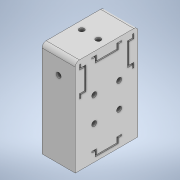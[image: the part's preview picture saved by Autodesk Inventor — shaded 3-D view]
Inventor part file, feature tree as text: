
AUTODESK INVENTOR PART (.ipt)
format: ipt  version: 2021 (Build 250183000, 183)  size: 275,968 bytes
history: native  units: mm
features: extrude x4, sketch x4, other x3
ambient origin geometry x8: Origin, YZ Plane, XZ Plane, XY Plane, X Axis, Y Axis, Z Axis, Center Point
bodies: Solid1 (feature_tree)
feature tree (11):
  other  "din_connector.ipt"
  extrude  "Extrusion1"  Depth=10.0mm TaperAngle=0.0deg
  extrude  "Extrusion2"  TaperAngle=0.0deg  [1 undecoded]
  extrude  "Extrusion3"  Depth=15.0mm
  extrude  "Extrusion4"  Depth=10.0mm
  other  "Solid1::din_connector.ipt"
  other  "TaggingFeature1"
  sketch  "Sketch1"  dims[d0=10.0mm d1=10.0mm d2=0.0mm]
  sketch  "Sketch2"  dims[d3=10.0mm d4=0.0mm d5=0.0mm d6=0.0mm]
  sketch  "Sketch3"  dims[d7=15.0mm d8=15.0mm]
  sketch  "Sketch4"  dims[d9=15.0mm d10=15.0mm d11=30.0mm d12=6.1mm d13=6.1mm d14=6.1mm d15=6.1mm d16=10.0mm d17=0.0mm]
note: 1 required parameter value undecoded (feature->parameter linkage not recoverable at this tier; creation-order binding heuristic only, values carry confidence <= 0.55)
